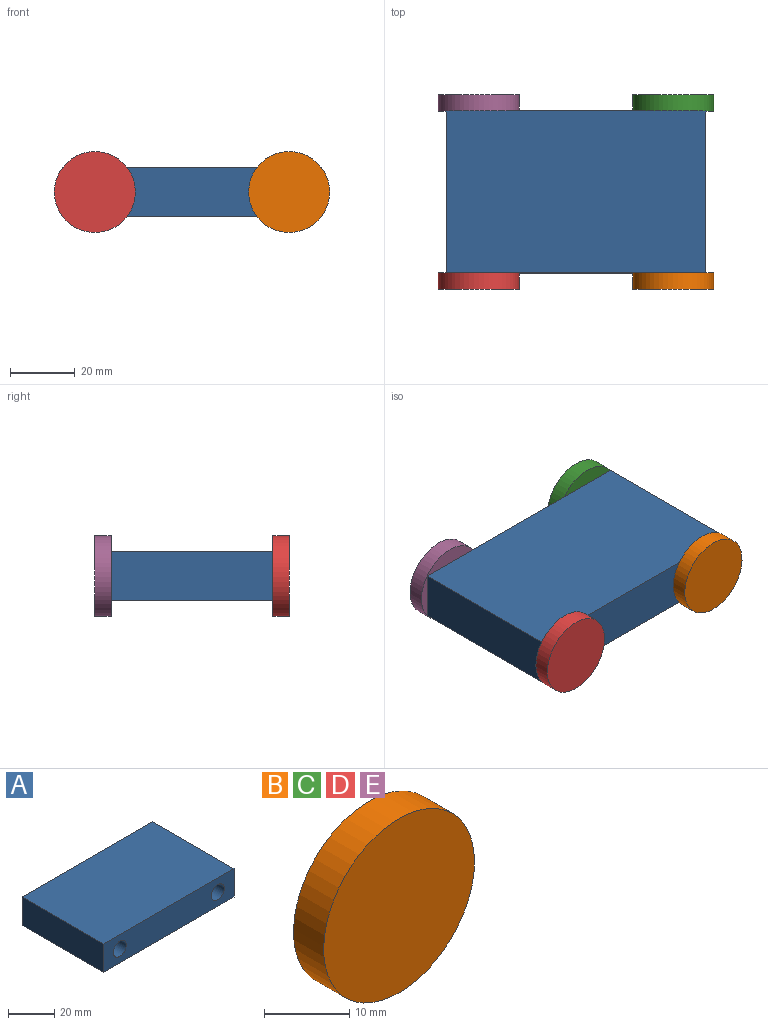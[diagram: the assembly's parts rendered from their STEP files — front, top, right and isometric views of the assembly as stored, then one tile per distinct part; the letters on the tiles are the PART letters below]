
ASSEMBLY  parts=5 mates=4
PART A: 8 faces, bbox 80x50x15 mm
  f0: plane 80x15mm, normal (0,1,0), area 1099.5mm2, adj f1,f3,f4,f5,f6,f7
  f1: plane 50x15mm, normal (-1,0,0), area 750mm2, adj f0,f2,f4,f5
  f2: plane 80x15mm, normal (0,-1,0), area 1099.5mm2, adj f1,f3,f4,f5,f6,f7
  f3: plane 50x15mm, normal (1,0,0), area 750mm2, adj f0,f2,f4,f5
  f4: plane 80x50mm, normal (0,0,1), area 4000mm2, adj f0,f1,f2,f3
  f5: plane 80x50mm, normal (0,0,-1), area 4000mm2, adj f0,f1,f2,f3
  f6: cylinder r=4mm len=50mm, axis (0,-1,0), area 1256.6mm2, adj f0,f2
  f7: cylinder r=4mm len=50mm, axis (0,-1,0), area 1256.6mm2, adj f0,f2
PART B: 3 faces, bbox 25x5x25 mm
  f0: cylinder r=12.5mm len=25mm, axis (0,1,0), area 392.7mm2, adj f1,f2
  f1: plane 25x25mm, normal (0,-1,0), area 490.9mm2, adj f0
  f2: plane 25x25mm, normal (0,1,0), area 490.9mm2, adj f0
PART C: same geometry as B
PART D: same geometry as B
PART E: same geometry as B
PLACE A t=(6.14,22.37,26.72)mm
PLACE B rot(axis=(1,0,0),180deg) t=(30.44,-6.93,34.22)mm
PLACE C rot(axis=(1,0,0),180deg) t=(30.44,48.07,34.22)mm
PLACE D rot(axis=(1,0,0),180deg) t=(-29.56,-6.93,34.22)mm
PLACE E rot(axis=(1,0,0),180deg) t=(-29.56,48.07,34.22)mm
MATE revolute E.f0 <-> A.f7  axis (0,-1,0) through (-29.56,48.07,34.22)mm
MATE revolute B.f0 <-> A.f6  axis (0,1,0) through (30.44,-1.93,34.22)mm
MATE revolute D.f0 <-> A.f7  axis (0,1,0) through (-29.56,-1.93,34.22)mm
MATE revolute C.f0 <-> A.f6  axis (0,-1,0) through (30.44,48.07,34.22)mm
